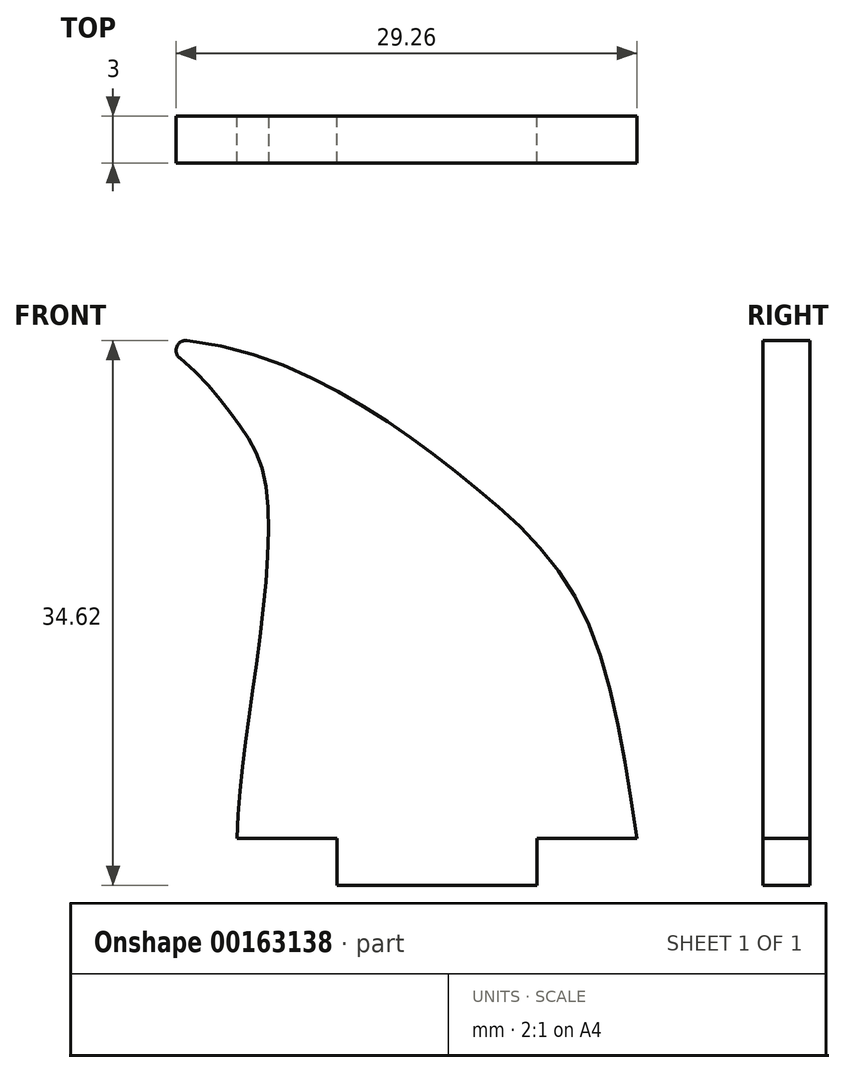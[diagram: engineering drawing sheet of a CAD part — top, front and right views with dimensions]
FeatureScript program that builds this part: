
annotation { "Feature Type Name" : "Feature", "Feature Type Description" : "" }
export const myFeature = defineFeature(function(context is Context, id is Id, definition is map)
    precondition{}
    {
        {
            var Q0;
            Q0=qCreatedBy(makeId("Front.planeOp"),FACE);
            var sketch = newSketch(context, id + "F0", { "sketchPlane" : qUnion([Q0])});
            skLineSegment(sketch, "E0.bottom", {"start": v(-6.35, 1.5) * mm, "end": v(6.35, 1.5) * mm, "construction": true});
            skLineSegment(sketch, "E0.top", {"start": v(-6.35, -1.5) * mm, "end": v(6.35, -1.5) * mm});
            skLineSegment(sketch, "E0.left", {"start": v(-6.35, 1.5) * mm, "end": v(-6.35, -1.5) * mm});
            skLineSegment(sketch, "E0.right", {"start": v(6.35, 1.5) * mm, "end": v(6.35, -1.5) * mm});
            skPoint(sketch, "E0.middle", {"position": v(0, 0) * mm});
            skLineSegment(sketch, "E1", {"start": v(-6.35, 1.5) * mm, "end": v(-12.7, 1.5) * mm});
            skLineSegment(sketch, "E2", {"start": v(6.35, 1.5) * mm, "end": v(12.7, 1.5) * mm});
            skFitSpline(sketch, "E3", {"points": [v(-18.28, 33.25) * mm, v(-6.02, 29.72) * mm, v(1.92, 24.2) * mm, v(8.9, 16.62) * mm, v(12.7, 1.5) * mm], "startDerivative": vector(56.84, 0) * mm, "endDerivative": vector(8.67, -59.39) * mm});
            skFitSpline(sketch, "E4", {"points": [v(-18.28, 33.25) * mm, v(-13.1, 28.52) * mm, v(-10.95, 24.31) * mm, v(-11.43, 12.9) * mm, v(-12.7, 1.5) * mm], "startDerivative": vector(33.6, -17.56) * mm, "endDerivative": vector(-1.16, -36.16) * mm});
            skSolve(sketch);
        }
        {
            var Q0;
            Q0 = qSketchRegion(id + "F0", true);
            extrude(context, id + "F1", {"entities" : qUnion([Q0]), "depth" : 3 * mm});
        }
        {
            var Q0;
            Q0=makeQuery(id+"F1.opExtrude","SWEPT_EDGE",EDGE,{"disambiguationData":[OSD([sQuery(id+"F0.wireOp",EDGE,"E3"),sQuery(id+"F0.wireOp",EDGE,"E4")])]});
            fillet(context, id + "F2", {"entities" : qUnion([Q0]), "radius" : 0.64 * mm, "tangentPropagation" : true, "allowEdgeOverflow" : false});
        }
    });
